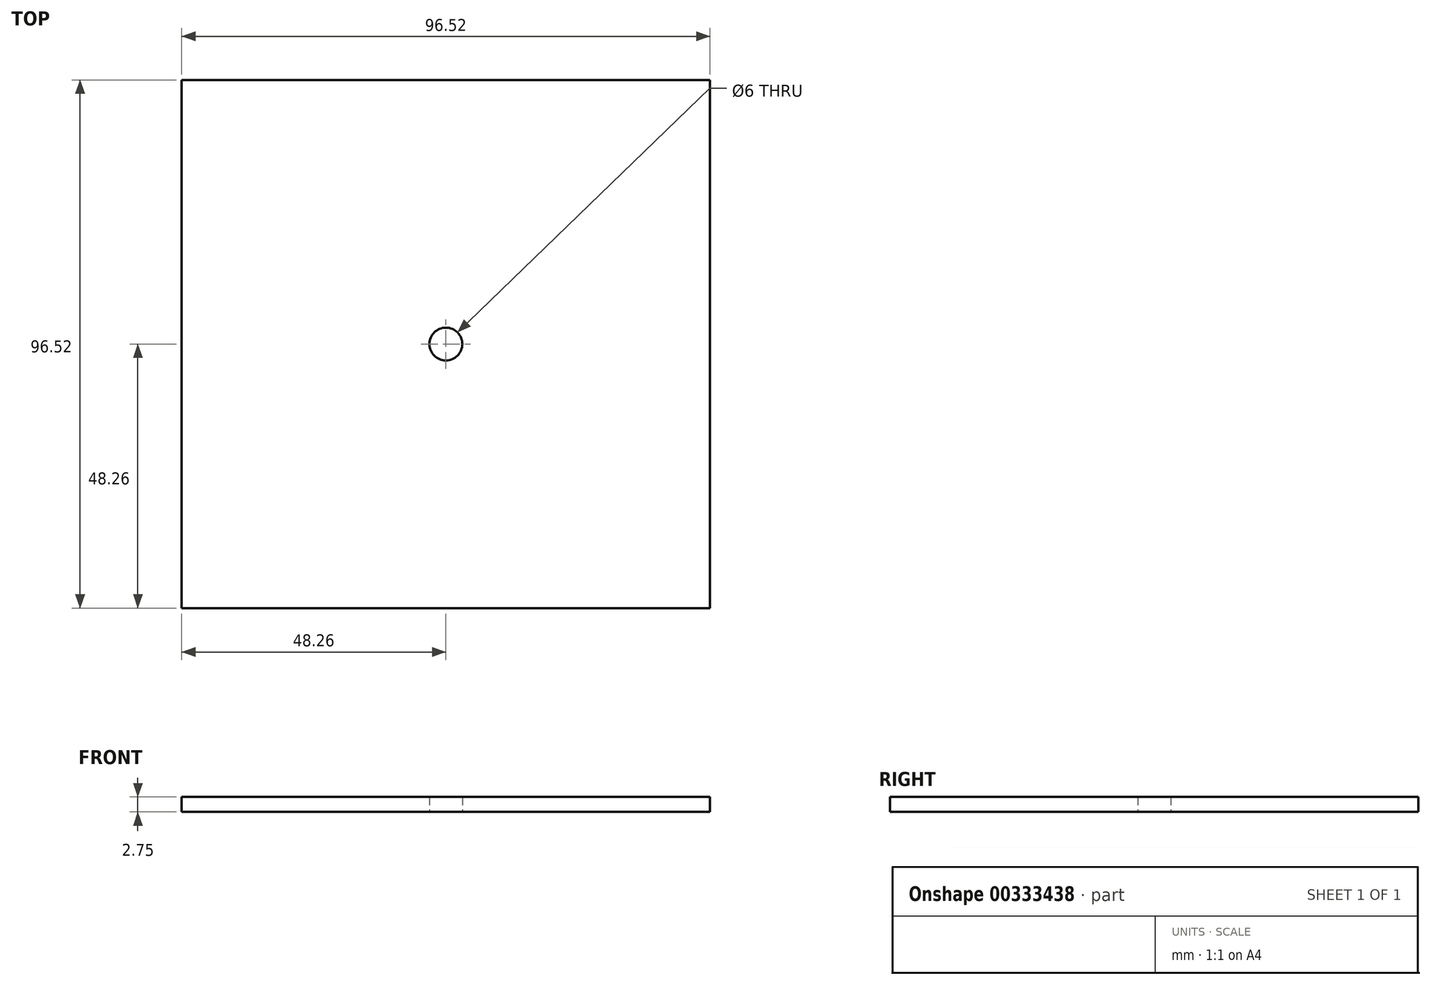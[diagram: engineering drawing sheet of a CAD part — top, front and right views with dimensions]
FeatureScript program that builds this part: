
annotation { "Feature Type Name" : "Feature", "Feature Type Description" : "" }
export const myFeature = defineFeature(function(context is Context, id is Id, definition is map)
    precondition{}
    {
        {
            var Q0;
            Q0=qCreatedBy(makeId("Top.planeOp"),FACE);
            var sketch = newSketch(context, id + "F0", { "sketchPlane" : qUnion([Q0])});
            skLineSegment(sketch, "E0.bottom", {"start": v(0, 0) * mm, "end": v(96.52, 0) * mm});
            skLineSegment(sketch, "E0.top", {"start": v(0, 96.52) * mm, "end": v(96.52, 96.52) * mm});
            skLineSegment(sketch, "E0.left", {"start": v(0, 0) * mm, "end": v(0, 96.52) * mm});
            skLineSegment(sketch, "E0.right", {"start": v(96.52, 0) * mm, "end": v(96.52, 96.52) * mm});
            skCircle(sketch, "E1", {"center": v(48.26, 48.26) * mm, "radius": 3 * mm});
            skSolve(sketch);
        }
        {
            var Q0;
            Q0=makeQuery(id+"F0.imprint","IMPRINT",FACE,{"disambiguationData":[TD([[makeQuery(id+"F0.imprint","IMPRINT",EDGE,{"derivedFrom":sQuery(id+"F0.wireOp",EDGE,"E0.bottom")}),1.0]])]});
            extrude(context, id + "F1", {"entities" : qUnion([Q0]), "depth" : 2.75 * mm});
        }
    });
